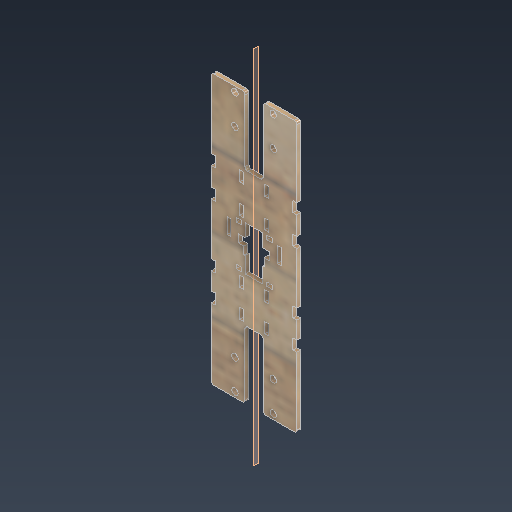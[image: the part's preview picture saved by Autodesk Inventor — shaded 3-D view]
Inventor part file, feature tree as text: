
AUTODESK INVENTOR PART (.ipt)
format: ipt  version: 2025.3 (Build 293356000, 356)  size: 381,440 bytes
history: native  units: mm
features: sketch x3, extrude x2, other x1
ambient origin geometry x8: Origin, YZ Plane, XZ Plane, XY Plane, X Axis, Y Axis, Z Axis, Center Point
bodies: Body1 (feature_tree)
feature tree (6):
  other  "實體1"
  extrude  "擠出1"  Depth=66.0mm
  sketch  "草圖3"
  extrude  "擠出4"  Depth=208.0mm
  sketch  "草圖1"
  sketch  "草圖5"
